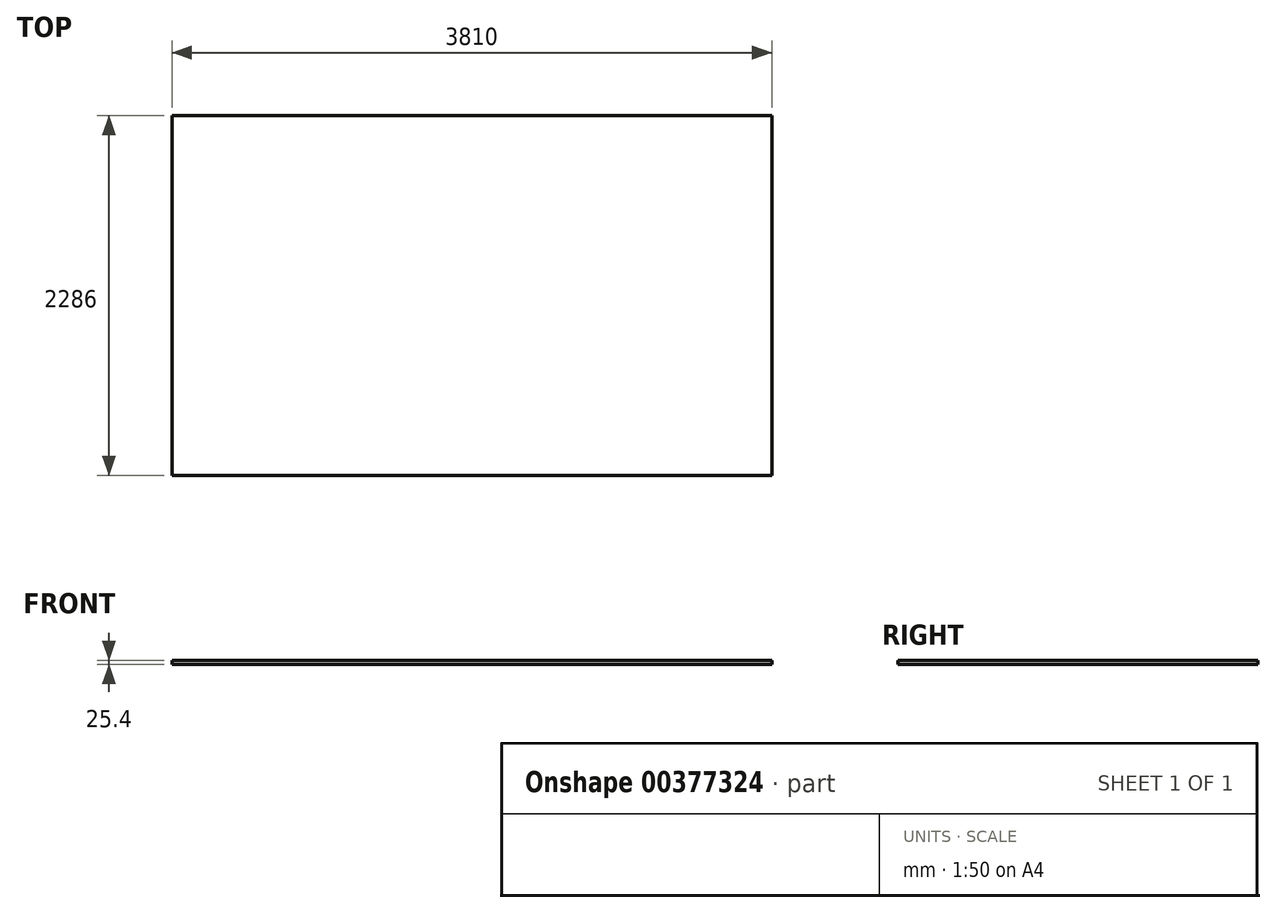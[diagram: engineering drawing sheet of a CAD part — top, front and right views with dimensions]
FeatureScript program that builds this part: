
annotation { "Feature Type Name" : "Feature", "Feature Type Description" : "" }
export const myFeature = defineFeature(function(context is Context, id is Id, definition is map)
    precondition{}
    {
        {
            var Q0;
            Q0=qCreatedBy(makeId("Top.planeOp"),FACE);
            var sketch = newSketch(context, id + "F0", { "sketchPlane" : qUnion([Q0])});
            skLineSegment(sketch, "E0.bottom", {"start": v(0, 0) * mm, "end": v(-3810, 0) * mm});
            skLineSegment(sketch, "E0.top", {"start": v(0, 2286) * mm, "end": v(-3810, 2286) * mm});
            skLineSegment(sketch, "E0.left", {"start": v(0, 0) * mm, "end": v(0, 2286) * mm});
            skLineSegment(sketch, "E0.right", {"start": v(-3810, 0) * mm, "end": v(-3810, 2286) * mm});
            skSolve(sketch);
        }
        {
            var Q0;
            Q0 = qSketchRegion(id + "F0", true);
            extrude(context, id + "F1", {"entities" : qUnion([Q0]), "depth" : 25.4 * mm});
        }
    });
